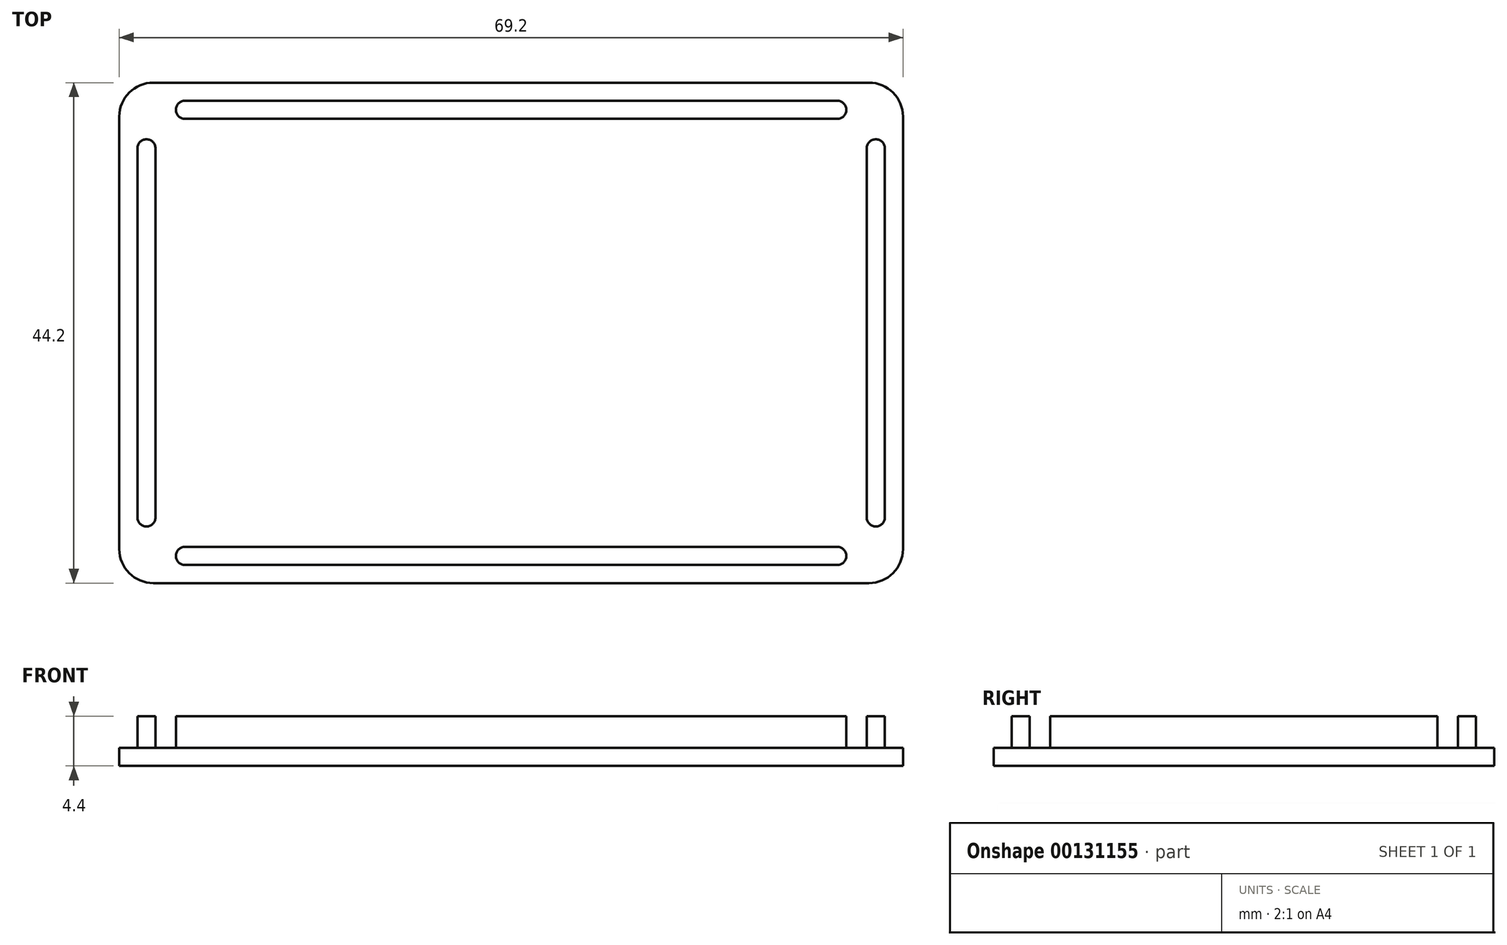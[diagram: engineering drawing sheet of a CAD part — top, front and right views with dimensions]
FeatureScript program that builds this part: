
annotation { "Feature Type Name" : "Feature", "Feature Type Description" : "" }
export const myFeature = defineFeature(function(context is Context, id is Id, definition is map)
    precondition{}
    {
        {
            var Q0;
            Q0=qCreatedBy(makeId("Top.planeOp"),FACE);
            var sketch = newSketch(context, id + "F0", { "sketchPlane" : qUnion([Q0])});
            skLineSegment(sketch, "E0.bottom", {"start": v(34.6, -22.1) * mm, "end": v(-34.6, -22.1) * mm});
            skLineSegment(sketch, "E0.top", {"start": v(34.6, 22.1) * mm, "end": v(-34.6, 22.1) * mm});
            skLineSegment(sketch, "E0.left", {"start": v(34.6, -22.1) * mm, "end": v(34.6, 22.1) * mm});
            skLineSegment(sketch, "E0.right", {"start": v(-34.6, -22.1) * mm, "end": v(-34.6, 22.1) * mm});
            skPoint(sketch, "E0.middle", {"position": v(0, 0) * mm});
            skSolve(sketch);
        }
        {
            var Q0;
            Q0 = qSketchRegion(id + "F0", true);
            extrude(context, id + "F1", {"entities" : qUnion([Q0]), "depth" : 1.6 * mm});
        }
        {
            var Q0;
            Q0=makeQuery(id+"F1.opExtrude","CAP_FACE",FACE,{"disambiguationData":[OSD([sQuery(id+"F0.wireOp",EDGE,"E0.bottom"),sQuery(id+"F0.wireOp",EDGE,"E0.top"),sQuery(id+"F0.wireOp",EDGE,"E0.left"),sQuery(id+"F0.wireOp",EDGE,"E0.right")])],"isStart":false});
            var sketch = newSketch(context, id + "F2", { "sketchPlane" : qUnion([Q0])});
            skLineSegment(sketch, "E1.bottom", {"start": v(-29.6, 20.5) * mm, "end": v(29.6, 20.5) * mm});
            skLineSegment(sketch, "E1.top", {"start": v(-29.6, 18.9) * mm, "end": v(29.6, 18.9) * mm});
            skLineSegment(sketch, "E1.left", {"start": v(-29.6, 20.5) * mm, "end": v(-29.6, 18.9) * mm});
            skLineSegment(sketch, "E1.right", {"start": v(29.6, 20.5) * mm, "end": v(29.6, 18.9) * mm});
            skLineSegment(sketch, "E2", {"start": v(-34.6, 0) * mm, "end": v(34.6, 0) * mm, "construction": true});
            skLineSegment(sketch, "E3.MirrorCS", {"start": v(-29.6, -20.5) * mm, "end": v(-29.6, -18.9) * mm});
            skLineSegment(sketch, "E4.MirrorCS", {"start": v(29.6, -20.5) * mm, "end": v(29.6, -18.9) * mm});
            skLineSegment(sketch, "E5.MirrorCS", {"start": v(-29.6, -20.5) * mm, "end": v(29.6, -20.5) * mm});
            skLineSegment(sketch, "E6.MirrorCS", {"start": v(-29.6, -18.9) * mm, "end": v(29.6, -18.9) * mm});
            skLineSegment(sketch, "E7", {"start": v(0, 22.1) * mm, "end": v(0, -22.1) * mm, "construction": true});
            skLineSegment(sketch, "E8.bottom", {"start": v(-33, 17.1) * mm, "end": v(-31.4, 17.1) * mm});
            skLineSegment(sketch, "E8.top", {"start": v(-33, -17.1) * mm, "end": v(-31.4, -17.1) * mm});
            skLineSegment(sketch, "E8.left", {"start": v(-33, 17.1) * mm, "end": v(-33, -17.1) * mm});
            skLineSegment(sketch, "E8.right", {"start": v(-31.4, 17.1) * mm, "end": v(-31.4, -17.1) * mm});
            skLineSegment(sketch, "E9.MirrorCS", {"start": v(33, -17.1) * mm, "end": v(31.4, -17.1) * mm});
            skLineSegment(sketch, "E10.MirrorCS", {"start": v(33, 17.1) * mm, "end": v(31.4, 17.1) * mm});
            skLineSegment(sketch, "E11.MirrorCS", {"start": v(31.4, 17.1) * mm, "end": v(31.4, -17.1) * mm});
            skLineSegment(sketch, "E12.MirrorCS", {"start": v(33, 17.1) * mm, "end": v(33, -17.1) * mm});
            skSolve(sketch);
        }
        {
            var Q0;
            Q0=makeQuery(id+"F2.imprint","IMPRINT",FACE,{"disambiguationData":[TD([[makeQuery(id+"F2.imprint","IMPRINT",EDGE,{"derivedFrom":sQuery(id+"F2.wireOp",EDGE,"E3.MirrorCS")}),-1.0]])]});
            var Q1;
            Q1=makeQuery(id+"F2.imprint","IMPRINT",FACE,{"disambiguationData":[TD([[makeQuery(id+"F2.imprint","IMPRINT",EDGE,{"derivedFrom":sQuery(id+"F2.wireOp",EDGE,"E8.bottom")}),-1.0]])]});
            var Q2;
            Q2=makeQuery(id+"F2.imprint","IMPRINT",FACE,{"disambiguationData":[TD([[makeQuery(id+"F2.imprint","IMPRINT",EDGE,{"derivedFrom":sQuery(id+"F2.wireOp",EDGE,"E9.MirrorCS")}),-1.0]])]});
            var Q3;
            Q3=makeQuery(id+"F2.imprint","IMPRINT",FACE,{"disambiguationData":[TD([[makeQuery(id+"F2.imprint","IMPRINT",EDGE,{"derivedFrom":sQuery(id+"F2.wireOp",EDGE,"E1.bottom")}),-1.0]])]});
            extrude(context, id + "F3", {"entities" : qUnion([Q0, Q1, Q2, Q3]), "operationType" : NewBodyOperationType.ADD, "depth" : 2.8 * mm});
        }
        {
            var Q0;
            Q0=makeQuery(id+"F1.opExtrude","SWEPT_EDGE",EDGE,{"disambiguationData":[OSD([sQuery(id+"F0.wireOp",EDGE,"E0.bottom"),sQuery(id+"F0.wireOp",EDGE,"E0.left")])]});
            var Q1;
            Q1=makeQuery(id+"F1.opExtrude","SWEPT_EDGE",EDGE,{"disambiguationData":[OSD([sQuery(id+"F0.wireOp",EDGE,"E0.top"),sQuery(id+"F0.wireOp",EDGE,"E0.left")])]});
            var Q2;
            Q2=makeQuery(id+"F1.opExtrude","SWEPT_EDGE",EDGE,{"disambiguationData":[OSD([sQuery(id+"F0.wireOp",EDGE,"E0.bottom"),sQuery(id+"F0.wireOp",EDGE,"E0.right")])]});
            var Q3;
            Q3=makeQuery(id+"F1.opExtrude","SWEPT_EDGE",EDGE,{"disambiguationData":[OSD([sQuery(id+"F0.wireOp",EDGE,"E0.top"),sQuery(id+"F0.wireOp",EDGE,"E0.right")])]});
            fillet(context, id + "F4", {"entities" : qUnion([Q0, Q1, Q2, Q3]), "radius" : 3 * mm, "tangentPropagation" : true, "allowEdgeOverflow" : false});
        }
        {
            var Q0;
            Q0=makeQuery(id+"F3.opExtrude","SWEPT_EDGE",EDGE,{"disambiguationData":[OSD([sQuery(id+"F2.wireOp",EDGE,"E4.MirrorCS"),sQuery(id+"F2.wireOp",EDGE,"E5.MirrorCS")])]});
            var Q1;
            Q1=makeQuery(id+"F3.opExtrude","SWEPT_EDGE",EDGE,{"disambiguationData":[OSD([sQuery(id+"F2.wireOp",EDGE,"E4.MirrorCS"),sQuery(id+"F2.wireOp",EDGE,"E6.MirrorCS")])]});
            var Q2;
            Q2=makeQuery(id+"F3.opExtrude","SWEPT_EDGE",EDGE,{"disambiguationData":[OSD([sQuery(id+"F2.wireOp",EDGE,"E9.MirrorCS"),sQuery(id+"F2.wireOp",EDGE,"E12.MirrorCS")])]});
            var Q3;
            Q3=makeQuery(id+"F3.opExtrude","SWEPT_EDGE",EDGE,{"disambiguationData":[OSD([sQuery(id+"F2.wireOp",EDGE,"E9.MirrorCS"),sQuery(id+"F2.wireOp",EDGE,"E11.MirrorCS")])]});
            var Q4;
            Q4=makeQuery(id+"F3.opExtrude","SWEPT_EDGE",EDGE,{"disambiguationData":[OSD([sQuery(id+"F2.wireOp",EDGE,"E1.top"),sQuery(id+"F2.wireOp",EDGE,"E1.right")])]});
            var Q5;
            Q5=makeQuery(id+"F3.opExtrude","SWEPT_EDGE",EDGE,{"disambiguationData":[OSD([sQuery(id+"F2.wireOp",EDGE,"E1.bottom"),sQuery(id+"F2.wireOp",EDGE,"E1.right")])]});
            var Q6;
            Q6=makeQuery(id+"F3.opExtrude","SWEPT_EDGE",EDGE,{"disambiguationData":[OSD([sQuery(id+"F2.wireOp",EDGE,"E8.top"),sQuery(id+"F2.wireOp",EDGE,"E8.left")])]});
            var Q7;
            Q7=makeQuery(id+"F3.opExtrude","SWEPT_EDGE",EDGE,{"disambiguationData":[OSD([sQuery(id+"F2.wireOp",EDGE,"E8.bottom"),sQuery(id+"F2.wireOp",EDGE,"E8.right")])]});
            var Q8;
            Q8=makeQuery(id+"F3.opExtrude","SWEPT_EDGE",EDGE,{"disambiguationData":[OSD([sQuery(id+"F2.wireOp",EDGE,"E8.top"),sQuery(id+"F2.wireOp",EDGE,"E8.right")])]});
            var Q9;
            Q9=makeQuery(id+"F3.opExtrude","SWEPT_EDGE",EDGE,{"disambiguationData":[OSD([sQuery(id+"F2.wireOp",EDGE,"E1.top"),sQuery(id+"F2.wireOp",EDGE,"E1.left")])]});
            var Q10;
            Q10=makeQuery(id+"F3.opExtrude","SWEPT_EDGE",EDGE,{"disambiguationData":[OSD([sQuery(id+"F2.wireOp",EDGE,"E10.MirrorCS"),sQuery(id+"F2.wireOp",EDGE,"E11.MirrorCS")])]});
            var Q11;
            Q11=makeQuery(id+"F3.opExtrude","SWEPT_EDGE",EDGE,{"disambiguationData":[OSD([sQuery(id+"F2.wireOp",EDGE,"E10.MirrorCS"),sQuery(id+"F2.wireOp",EDGE,"E12.MirrorCS")])]});
            var Q12;
            Q12=makeQuery(id+"F3.opExtrude","SWEPT_EDGE",EDGE,{"disambiguationData":[OSD([sQuery(id+"F2.wireOp",EDGE,"E8.bottom"),sQuery(id+"F2.wireOp",EDGE,"E8.left")])]});
            var Q13;
            Q13=makeQuery(id+"F3.opExtrude","SWEPT_EDGE",EDGE,{"disambiguationData":[OSD([sQuery(id+"F2.wireOp",EDGE,"E3.MirrorCS"),sQuery(id+"F2.wireOp",EDGE,"E6.MirrorCS")])]});
            var Q14;
            Q14=makeQuery(id+"F3.opExtrude","SWEPT_EDGE",EDGE,{"disambiguationData":[OSD([sQuery(id+"F2.wireOp",EDGE,"E1.bottom"),sQuery(id+"F2.wireOp",EDGE,"E1.left")])]});
            var Q15;
            Q15=makeQuery(id+"F3.opExtrude","SWEPT_EDGE",EDGE,{"disambiguationData":[OSD([sQuery(id+"F2.wireOp",EDGE,"E3.MirrorCS"),sQuery(id+"F2.wireOp",EDGE,"E5.MirrorCS")])]});
            fillet(context, id + "F5", {"entities" : qUnion([Q0, Q1, Q2, Q3, Q4, Q5, Q6, Q7, Q8, Q9, Q10, Q11, Q12, Q13, Q14, Q15]), "radius" : 0.8 * mm, "tangentPropagation" : true, "allowEdgeOverflow" : false});
        }
    });
